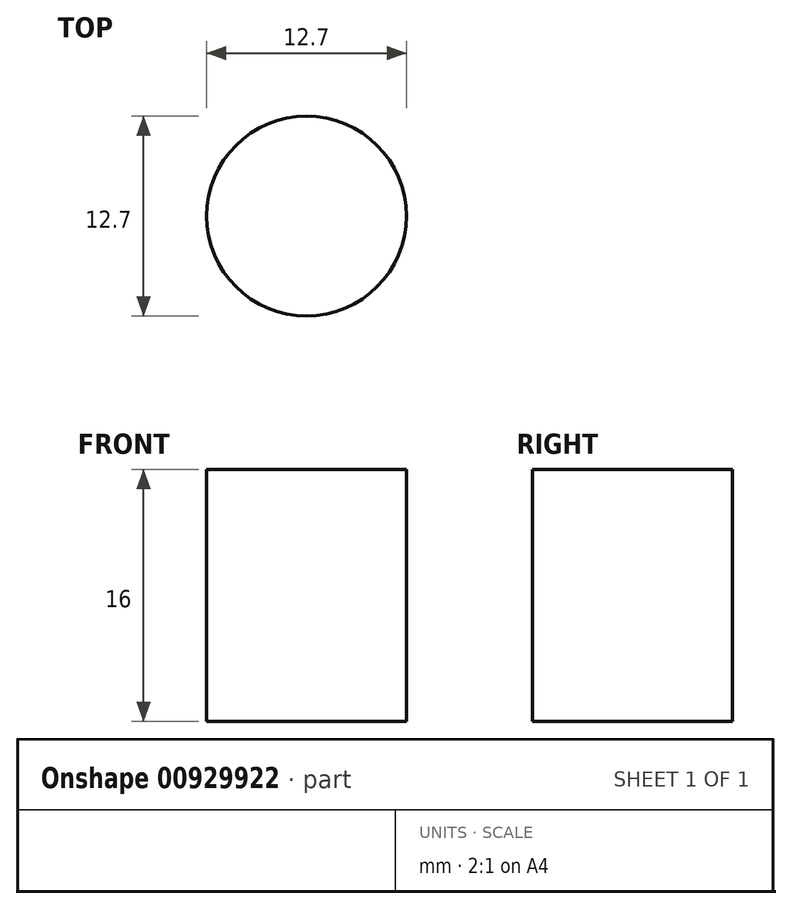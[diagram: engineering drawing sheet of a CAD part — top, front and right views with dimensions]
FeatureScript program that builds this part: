
annotation { "Feature Type Name" : "Feature", "Feature Type Description" : "" }
export const myFeature = defineFeature(function(context is Context, id is Id, definition is map)
    precondition{}
    {
        {
            var Q0;
            Q0=qCreatedBy(makeId("Top.planeOp"),FACE);
            var sketch = newSketch(context, id + "F0", { "sketchPlane" : qUnion([Q0])});
            skCircle(sketch, "E0", {"center": v(0, 0) * mm, "radius": 6.35 * mm});
            skSolve(sketch);
        }
        {
            var Q0;
            Q0 = qSketchRegion(id + "F0", true);
            extrude(context, id + "F1", {"entities" : qUnion([Q0]), "depth" : 16 * mm, "offsetDistance" : 25.4 * mm});
        }
    });
